# Revit family: FU_Stool_Sandler_Euthalia-181-41
name_source: partatom
category: Furniture
units: mm (PartAtom-declared; Revit-internal decimal feet)

## family parameters
Always vertical = Yes
Cut with Voids When Loaded = No
OmniClass Number = 23.40.20.00
OmniClass Title = General Furniture and Specialties
Room Calculation Point = No
Shared = No
Work Plane-Based = No

## types (1)
- FU_Stool_Sandler_Euthalia-181-41
    Default Elevation = 0 mm  [stored 0 ft]
    Depth = 520 mm  [stored 1.70604 ft]
    Description = Barstool in walnut or beech frame with upholstered seat. Footrest in stainless steel. This product has an extended lead time.
    Height = 1130 mm  [stored 3.70735 ft]
    Manufacturer = Sandler
    Model = Euthalia 181.41
    URL = https://www.sandlerseating.com
    Upholstery = Fabric - Mainline Flax - Upminster MLF20
    Width = 430 mm  [stored 1.41076 ft]
    Wood = Wood - Beech - Cherry Wood - V

note: [stored X ft] marks values corroborated as IEEE doubles in the binary element streams (Revit-internal decimal feet)

## geometry (parser evidence)
native form markers: Sweep x2
no freeform markers — native parametric forms only
